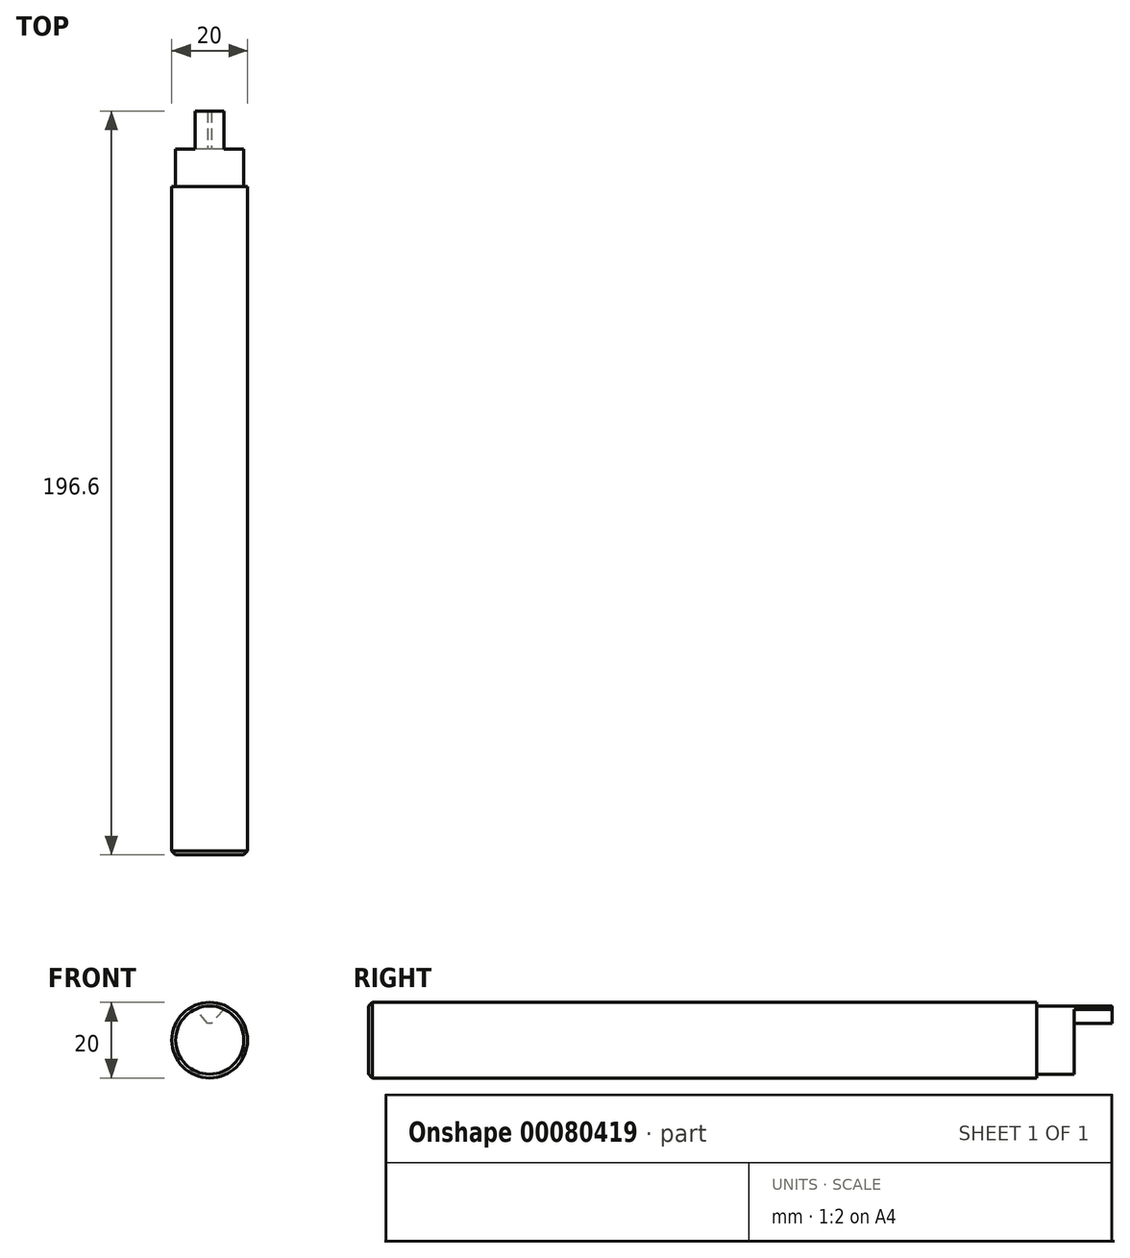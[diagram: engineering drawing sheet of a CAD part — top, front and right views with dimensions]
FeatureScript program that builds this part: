
annotation { "Feature Type Name" : "Feature", "Feature Type Description" : "" }
export const myFeature = defineFeature(function(context is Context, id is Id, definition is map)
    precondition{}
    {
        {
            var Q0;
            Q0=qCreatedBy(makeId("Front.planeOp"),FACE);
            var sketch = newSketch(context, id + "F0", { "sketchPlane" : qUnion([Q0])});
            skCircle(sketch, "E0", {"center": v(0, 0) * mm, "radius": 10 * mm});
            skSolve(sketch);
        }
        {
            var Q0;
            Q0 = qSketchRegion(id + "F0", true);
            extrude(context, id + "F1", {"entities" : qUnion([Q0]), "endBound" : BoundingType.SYMMETRIC, "depth" : (28.3 * 2 + 120) * mm});
        }
        {
            var Q0;
            Q0=makeQuery(id+"F1.opExtrude","CAP_FACE",FACE,{"disambiguationData":[OSD([sQuery(id+"F0.wireOp",EDGE,"E0")])],"isStart":true});
            var sketch = newSketch(context, id + "F2", { "sketchPlane" : qUnion([Q0])});
            skCircle(sketch, "E1", {"center": v(0, 0) * mm, "radius": 9 * mm});
            skSolve(sketch);
        }
        {
            var Q0;
            Q0 = qSketchRegion(id + "F2", true);
            extrude(context, id + "F3", {"entities" : qUnion([Q0]), "operationType" : NewBodyOperationType.ADD, "depth" : 10 * mm});
        }
        {
            var Q0;
            Q0=makeQuery(id+"F3.opExtrude","CAP_FACE",FACE,{"disambiguationData":[OSD([sQuery(id+"F2.wireOp",EDGE,"E1")])],"isStart":false});
            var sketch = newSketch(context, id + "F4", { "sketchPlane" : qUnion([Q0])});
            skLineSegment(sketch, "E2", {"start": v(-3.78, 8.17) * mm, "end": v(-0.5, 4.4) * mm});
            skLineSegment(sketch, "E3", {"start": v(-0.5, 4.4) * mm, "end": v(0.5, 4.4) * mm});
            skLineSegment(sketch, "E4", {"start": v(0.5, 4.4) * mm, "end": v(3.78, 8.17) * mm});
            skPoint(sketch, "E5", {"position": v(0, 4.4) * mm});
            skLineSegment(sketch, "E6", {"start": v(0, 0) * mm, "end": v(-5.9, 6.8) * mm, "construction": true});
            skLineSegment(sketch, "E7", {"start": v(-0.5, 4.4) * mm, "end": v(-4.28, 1.12) * mm, "construction": true});
            skLineSegment(sketch, "E8", {"start": v(-4.28, 1.12) * mm, "end": v(-7.55, 4.9) * mm, "construction": true});
            skPoint(sketch, "E9", {"position": v(-2.39, 2.75) * mm});
            skArc(sketch, "E10", {"start": v(-3.78, 8.17) * mm, "mid": v(0, 9) * mm, "end": v(3.78, 8.17) * mm});
            skSolve(sketch);
        }
        {
            var Q0;
            Q0 = qSketchRegion(id + "F4", true);
            extrude(context, id + "F5", {"entities" : qUnion([Q0]), "operationType" : NewBodyOperationType.ADD, "depth" : 10 * mm});
        }
        {
            var Q0;
            Q0=makeQuery(id+"F1.opExtrude","CAP_EDGE",EDGE,{"disambiguationData":[OSD([sQuery(id+"F0.wireOp",EDGE,"E0")])],"isStart":false});
            chamfer(context, id + "F6", {"entities" : qUnion([Q0]), "width" : 1 * mm, "tangentPropagation" : true});
        }
    });
